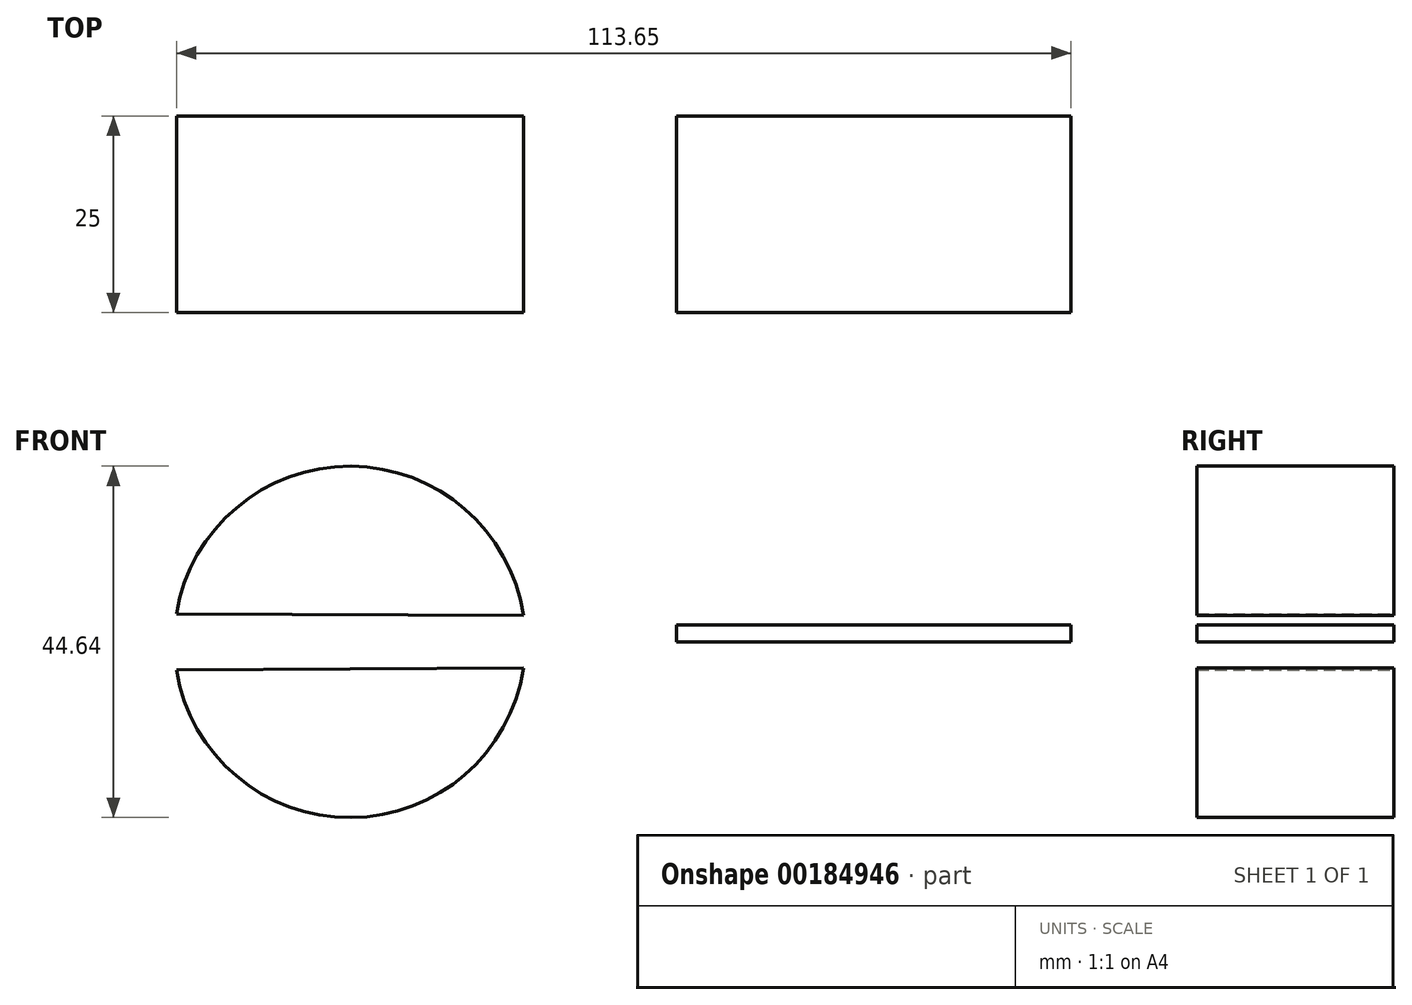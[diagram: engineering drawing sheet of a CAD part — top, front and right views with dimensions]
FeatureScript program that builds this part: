
annotation { "Feature Type Name" : "Feature", "Feature Type Description" : "" }
export const myFeature = defineFeature(function(context is Context, id is Id, definition is map)
    precondition{}
    {
        {
            var Q0;
            Q0=qCreatedBy(makeId("Front.planeOp"),FACE);
            var sketch = newSketch(context, id + "F0", { "sketchPlane" : qUnion([Q0])});
            skArc(sketch, "E0", {"start": v(-12.35, 3.33) * mm, "mid": v(-34.3, 22.32) * mm, "end": v(-56.45, 3.58) * mm});
            skLineSegment(sketch, "E1", {"start": v(-56.45, 3.58) * mm, "end": v(-12.35, 3.33) * mm});
            skLineSegment(sketch, "E2.MirrorCS", {"start": v(-56.45, -3.58) * mm, "end": v(-12.35, -3.33) * mm});
            skArc(sketch, "E3.MirrorCS", {"start": v(-12.35, -3.33) * mm, "mid": v(-34.3, -22.32) * mm, "end": v(-56.45, -3.58) * mm});
            skLineSegment(sketch, "E4.bottom", {"start": v(7.06, 2.14) * mm, "end": v(57.2, 2.14) * mm});
            skLineSegment(sketch, "E4.top", {"start": v(7.06, 0) * mm, "end": v(57.2, 0) * mm});
            skLineSegment(sketch, "E4.left", {"start": v(7.06, 2.14) * mm, "end": v(7.06, 0) * mm});
            skLineSegment(sketch, "E4.right", {"start": v(57.2, 2.14) * mm, "end": v(57.2, 0) * mm});
            skArc(sketch, "E5", {"start": v(105.04, 18.34) * mm, "mid": v(101.39, 31.98) * mm, "end": v(95.81, 44.95) * mm});
            skArc(sketch, "E6", {"start": v(92.22, 55.16) * mm, "mid": v(95.21, 54.23) * mm, "end": v(98.08, 52.94) * mm});
            skArc(sketch, "E7", {"start": v(106.52, 14.84) * mm, "mid": v(54.56, 18.58) * mm, "end": v(32.39, 65.7) * mm});
            skSolve(sketch);
        }
        {
            var Q0;
            Q0 = qSketchRegion(id + "F0", true);
            extrude(context, id + "F1", {"entities" : qUnion([Q0]), "depth" : 25 * mm});
        }
    });
